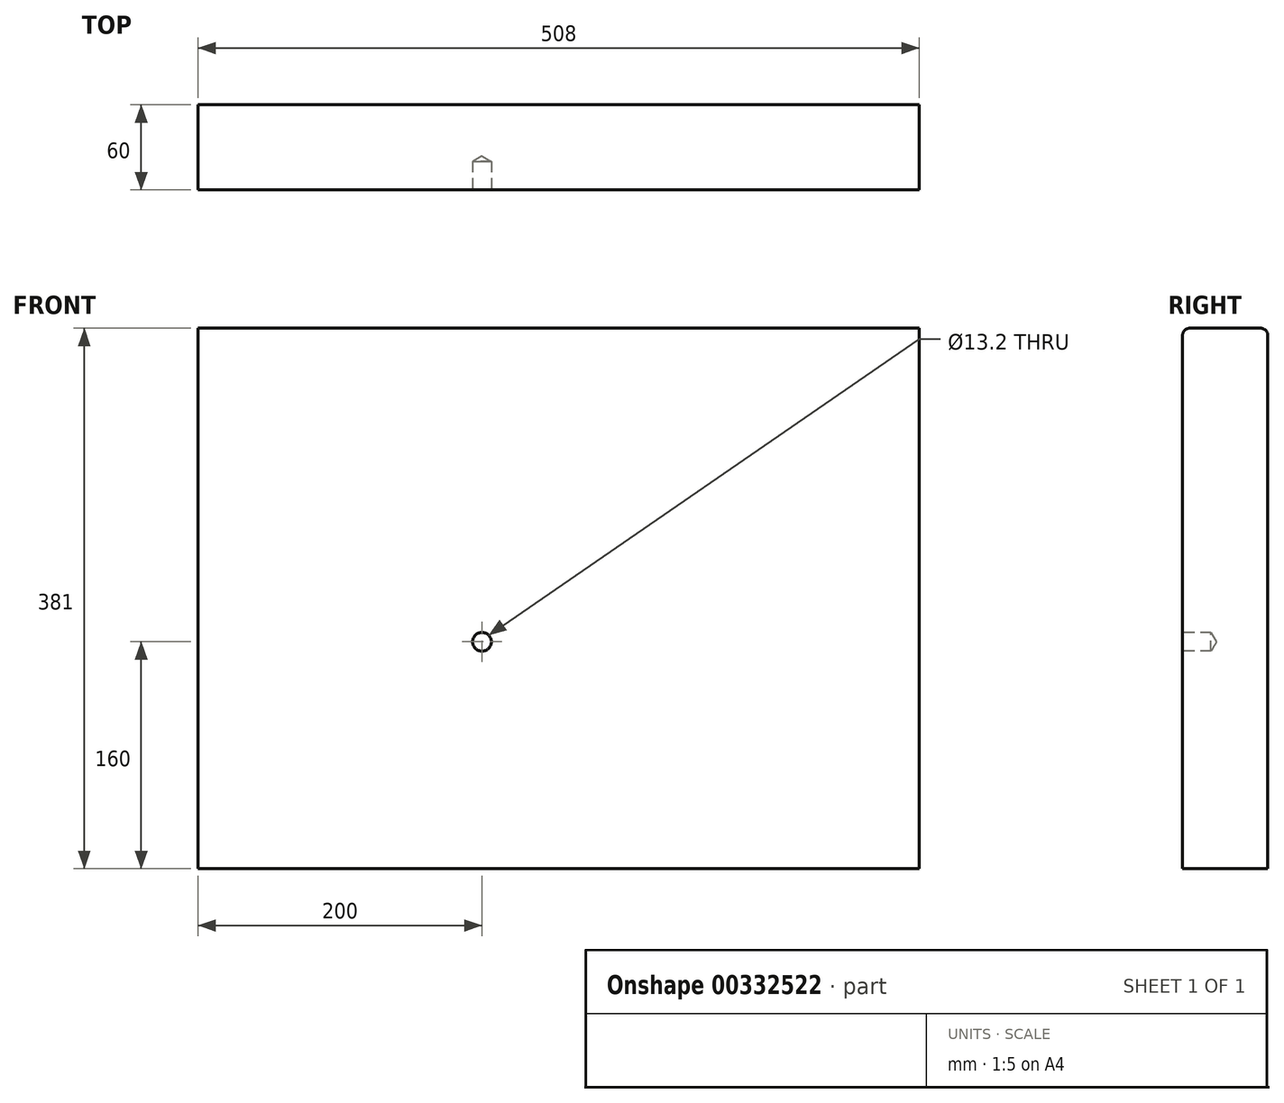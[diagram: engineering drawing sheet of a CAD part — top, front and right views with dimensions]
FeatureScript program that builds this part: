
annotation { "Feature Type Name" : "Feature", "Feature Type Description" : "" }
export const myFeature = defineFeature(function(context is Context, id is Id, definition is map)
    precondition{}
    {
        {
            var Q0;
            Q0=qCreatedBy(makeId("Front.planeOp"),FACE);
            var sketch = newSketch(context, id + "F0", { "sketchPlane" : qUnion([Q0])});
            skLineSegment(sketch, "E0", {"start": v(0, 0) * mm, "end": v(508, 0) * mm});
            skLineSegment(sketch, "E1", {"start": v(508, 0) * mm, "end": v(508, 381) * mm});
            skLineSegment(sketch, "E2", {"start": v(508, 381) * mm, "end": v(0, 381) * mm});
            skLineSegment(sketch, "E3", {"start": v(0, 381) * mm, "end": v(0, 0) * mm});
            skSolve(sketch);
        }
        {
            var Q0;
            Q0 = qSketchRegion(id + "F0", true);
            extrude(context, id + "F1", {"entities" : qUnion([Q0]), "depth" : 60 * mm});
        }
        {
            var Q0;
            Q0=makeQuery(id+"F1.opExtrude","CAP_FACE",FACE,{"disambiguationData":[OSD([sQuery(id+"F0.wireOp",EDGE,"E0"),sQuery(id+"F0.wireOp",EDGE,"E1"),sQuery(id+"F0.wireOp",EDGE,"E2"),sQuery(id+"F0.wireOp",EDGE,"E3")])],"isStart":false});
            var sketch = newSketch(context, id + "F2", { "sketchPlane" : qUnion([Q0])});
            skPoint(sketch, "E4", {"position": v(200, 160) * mm});
            skSolve(sketch);
        }
        {
            var Q0;
            Q0=sQuery(id+"F2.wireOp",VERTEX,"E4");
            var Q1;
            Q1=makeQuery(id+"F1.opExtrude","SWEPT_BODY",BODY,{"disambiguationData":[OSD([sQuery(id+"F0.wireOp",EDGE,"E0"),sQuery(id+"F0.wireOp",EDGE,"E1"),sQuery(id+"F0.wireOp",EDGE,"E2"),sQuery(id+"F0.wireOp",EDGE,"E3")])]});
            hole(context, id + "F3", {"style" : HoleStyle.SIMPLE, "endStyle" : HoleEndStyle.BLIND, "standardTappedOrClearance" : lookupTablePath({ "standard" : "ISO", "fit" : "Normal", "size" : "M12", "type" : "Clearance" }), "standardBlindInLast" : lookupTablePath({ "fit" : "Standard", "standard" : "ISO", "size" : "M12", "type" : "Clearance" }), "holeDiameter" : 13.2 * mm, "holeDepth" : 20 * mm, "tappedDepth" : 12 * mm, "tapClearance" : 3, "locations" : qUnion([Q0]), "scope" : qUnion([Q1])});
        }
        {
            var Q0;
            Q0=makeQuery(id+"F1.opExtrude","CAP_EDGE",EDGE,{"disambiguationData":[OSD([sQuery(id+"F0.wireOp",EDGE,"E2")])],"isStart":false});
            var Q1;
            Q1=makeQuery(id+"F1.opExtrude","CAP_EDGE",EDGE,{"disambiguationData":[OSD([sQuery(id+"F0.wireOp",EDGE,"E2")])],"isStart":true});
            fillet(context, id + "F4", {"entities" : qUnion([Q0, Q1]), "radius" : 5 * mm, "tangentPropagation" : true, "allowEdgeOverflow" : false});
        }
    });
